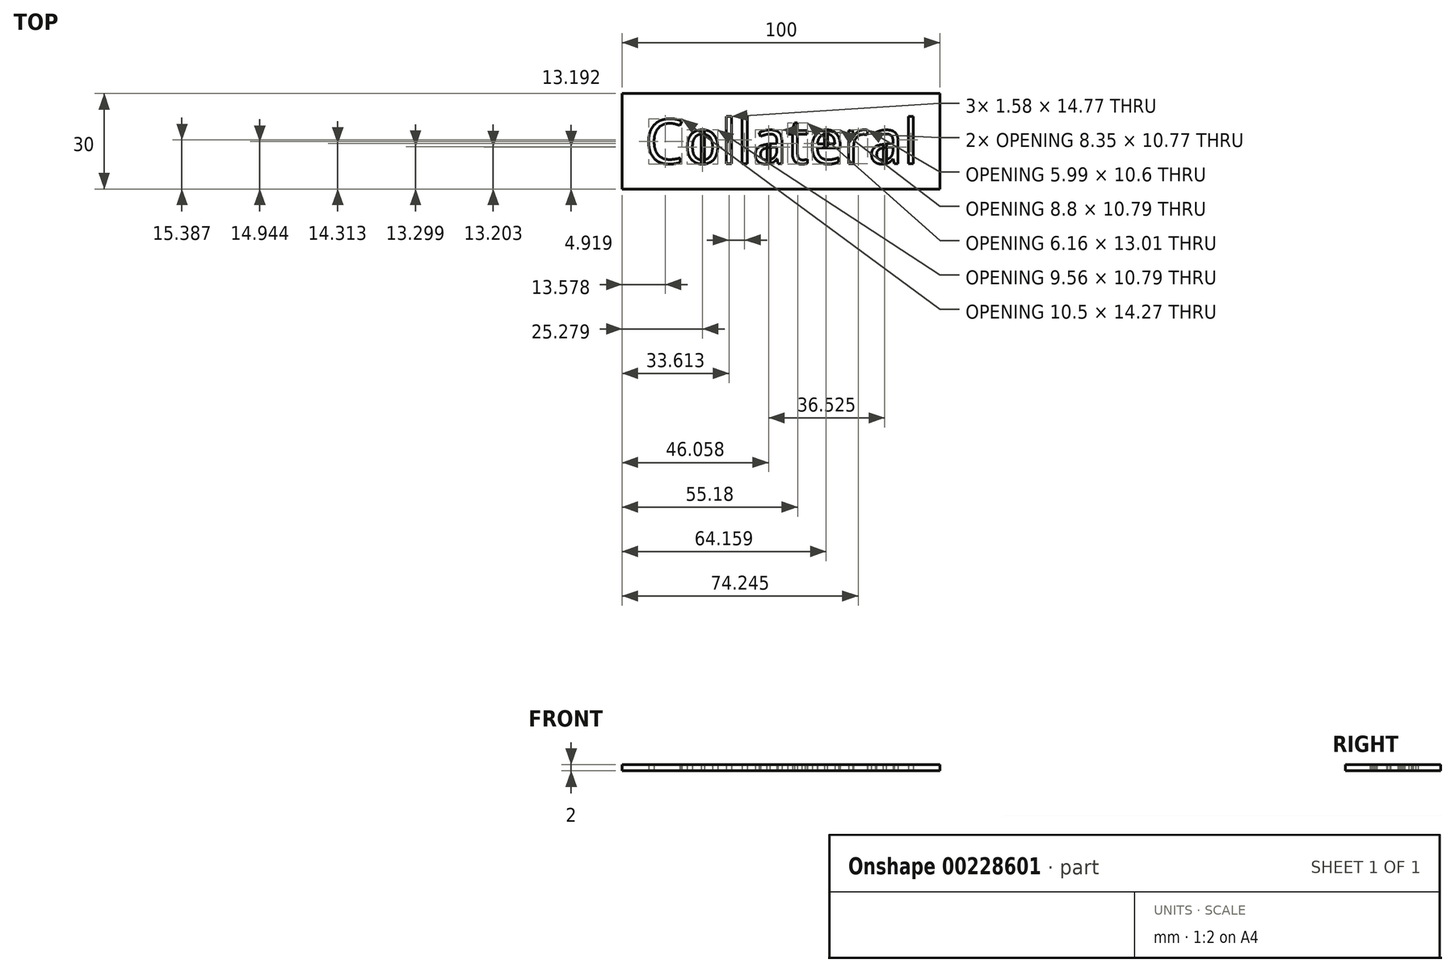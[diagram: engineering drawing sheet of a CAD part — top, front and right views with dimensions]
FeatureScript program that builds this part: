
annotation { "Feature Type Name" : "Feature", "Feature Type Description" : "" }
export const myFeature = defineFeature(function(context is Context, id is Id, definition is map)
    precondition{}
    {
        {
            assignVariable(context, id + "F0", {"name" : "thickness", "anyValue" : 2});
        }
        {
            var Q0;
            Q0=qCreatedBy(makeId("Top.planeOp"),FACE);
            var sketch = newSketch(context, id + "F1", { "sketchPlane" : qUnion([Q0])});
            skText(sketch, "E0", { "text": "Collateral", "fontName": "OpenSans-Regular.ttf"});
            skLineSegment(sketch, "E1.bottom", {"start": v(-51.22, 37.77) * mm, "end": v(48.78, 37.77) * mm});
            skLineSegment(sketch, "E1.top", {"start": v(-51.22, 7.77) * mm, "end": v(48.78, 7.77) * mm});
            skLineSegment(sketch, "E1.left", {"start": v(-51.22, 37.77) * mm, "end": v(-51.22, 7.77) * mm});
            skLineSegment(sketch, "E1.right", {"start": v(48.78, 37.77) * mm, "end": v(48.78, 7.77) * mm});
            const initialGuessF1  = {"E0": [-0.04408, 0.01577, 1, 0, 0.014]};
            skSetInitialGuess(sketch, initialGuessF1);
            skSolve(sketch);
        }
        {
            var Q0;
            Q0=makeQuery(id+"F1.imprint","IMPRINT",FACE,{"disambiguationData":[TD([[makeQuery(id+"F1.imprint","IMPRINT",EDGE,{"derivedFrom":sQuery(id+"F1.wireOp",EDGE,"E0.sketch_text.stroke-0")}),1.0]])]});
            var Q1;
            Q1=makeQuery(id+"F1.imprint","IMPRINT",FACE,{"disambiguationData":[TD([[makeQuery(id+"F1.imprint","IMPRINT",EDGE,{"derivedFrom":sQuery(id+"F1.wireOp",EDGE,"E0.sketch_text.stroke-59")}),1.0]])]});
            var Q2;
            Q2=makeQuery(id+"F1.imprint","IMPRINT",FACE,{"disambiguationData":[TD([[makeQuery(id+"F1.imprint","IMPRINT",EDGE,{"derivedFrom":sQuery(id+"F1.wireOp",EDGE,"E0.sketch_text.stroke-100")}),1.0]])]});
            var Q3;
            Q3=makeQuery(id+"F1.imprint","IMPRINT",FACE,{"disambiguationData":[TD([[makeQuery(id+"F1.imprint","IMPRINT",EDGE,{"derivedFrom":sQuery(id+"F1.wireOp",EDGE,"E0.sketch_text.stroke-137")}),1.0]])]});
            var Q4;
            Q4=makeQuery(id+"F1.imprint","IMPRINT",FACE,{"disambiguationData":[TD([[makeQuery(id+"F1.imprint","IMPRINT",EDGE,{"derivedFrom":sQuery(id+"F1.wireOp",EDGE,"E0.sketch_text.stroke-24")}),1.0]])]});
            extrude(context, id + "F2", {"entities" : qUnion([Q0, Q1, Q2, Q3, Q4]), "depth" : (getVariable(context, 'thickness')) * mm});
        }
        {
            var Q0;
            Q0=makeQuery(id+"F2.opExtrude","CAP_FACE",FACE,{"disambiguationData":[OSD([sQuery(id+"F1.wireOp",EDGE,"E0.sketch_text.stroke-0"),sQuery(id+"F1.wireOp",EDGE,"E0.sketch_text.stroke-1"),sQuery(id+"F1.wireOp",EDGE,"E0.sketch_text.stroke-2"),sQuery(id+"F1.wireOp",EDGE,"E0.sketch_text.stroke-3"),sQuery(id+"F1.wireOp",EDGE,"E0.sketch_text.stroke-4"),sQuery(id+"F1.wireOp",EDGE,"E0.sketch_text.stroke-5"),sQuery(id+"F1.wireOp",EDGE,"E0.sketch_text.stroke-6"),sQuery(id+"F1.wireOp",EDGE,"E0.sketch_text.stroke-7"),sQuery(id+"F1.wireOp",EDGE,"E0.sketch_text.stroke-8"),sQuery(id+"F1.wireOp",EDGE,"E0.sketch_text.stroke-9"),sQuery(id+"F1.wireOp",EDGE,"E0.sketch_text.stroke-10"),sQuery(id+"F1.wireOp",EDGE,"E0.sketch_text.stroke-11"),sQuery(id+"F1.wireOp",EDGE,"E0.sketch_text.stroke-12"),sQuery(id+"F1.wireOp",EDGE,"E0.sketch_text.stroke-13"),sQuery(id+"F1.wireOp",EDGE,"E0.sketch_text.stroke-14"),sQuery(id+"F1.wireOp",EDGE,"E0.sketch_text.stroke-15"),sQuery(id+"F1.wireOp",EDGE,"E0.sketch_text.stroke-16"),sQuery(id+"F1.wireOp",EDGE,"E0.sketch_text.stroke-17"),sQuery(id+"F1.wireOp",EDGE,"E0.sketch_text.stroke-18"),sQuery(id+"F1.wireOp",EDGE,"E0.sketch_text.stroke-19"),sQuery(id+"F1.wireOp",EDGE,"E0.sketch_text.stroke-20"),sQuery(id+"F1.wireOp",EDGE,"E0.sketch_text.stroke-21"),sQuery(id+"F1.wireOp",EDGE,"E0.sketch_text.stroke-22"),sQuery(id+"F1.wireOp",EDGE,"E0.sketch_text.stroke-23"),sQuery(id+"F1.wireOp",EDGE,"E0.sketch_text.stroke-32"),sQuery(id+"F1.wireOp",EDGE,"E0.sketch_text.stroke-33"),sQuery(id+"F1.wireOp",EDGE,"E0.sketch_text.stroke-34"),sQuery(id+"F1.wireOp",EDGE,"E0.sketch_text.stroke-35"),sQuery(id+"F1.wireOp",EDGE,"E0.sketch_text.stroke-36"),sQuery(id+"F1.wireOp",EDGE,"E0.sketch_text.stroke-37"),sQuery(id+"F1.wireOp",EDGE,"E0.sketch_text.stroke-38"),sQuery(id+"F1.wireOp",EDGE,"E0.sketch_text.stroke-39"),sQuery(id+"F1.wireOp",EDGE,"E0.sketch_text.stroke-40"),sQuery(id+"F1.wireOp",EDGE,"E0.sketch_text.stroke-41"),sQuery(id+"F1.wireOp",EDGE,"E0.sketch_text.stroke-42"),sQuery(id+"F1.wireOp",EDGE,"E0.sketch_text.stroke-43"),sQuery(id+"F1.wireOp",EDGE,"E0.sketch_text.stroke-44"),sQuery(id+"F1.wireOp",EDGE,"E0.sketch_text.stroke-45"),sQuery(id+"F1.wireOp",EDGE,"E0.sketch_text.stroke-46"),sQuery(id+"F1.wireOp",EDGE,"E0.sketch_text.stroke-47"),sQuery(id+"F1.wireOp",EDGE,"E0.sketch_text.stroke-48"),sQuery(id+"F1.wireOp",EDGE,"E0.sketch_text.stroke-49"),sQuery(id+"F1.wireOp",EDGE,"E0.sketch_text.stroke-50"),sQuery(id+"F1.wireOp",EDGE,"E0.sketch_text.stroke-51"),sQuery(id+"F1.wireOp",EDGE,"E0.sketch_text.stroke-52"),sQuery(id+"F1.wireOp",EDGE,"E0.sketch_text.stroke-53"),sQuery(id+"F1.wireOp",EDGE,"E0.sketch_text.stroke-54"),sQuery(id+"F1.wireOp",EDGE,"E0.sketch_text.stroke-55"),sQuery(id+"F1.wireOp",EDGE,"E0.sketch_text.stroke-56"),sQuery(id+"F1.wireOp",EDGE,"E0.sketch_text.stroke-57"),sQuery(id+"F1.wireOp",EDGE,"E0.sketch_text.stroke-58"),sQuery(id+"F1.wireOp",EDGE,"E0.sketch_text.stroke-67"),sQuery(id+"F1.wireOp",EDGE,"E0.sketch_text.stroke-68"),sQuery(id+"F1.wireOp",EDGE,"E0.sketch_text.stroke-69"),sQuery(id+"F1.wireOp",EDGE,"E0.sketch_text.stroke-70"),sQuery(id+"F1.wireOp",EDGE,"E0.sketch_text.stroke-71"),sQuery(id+"F1.wireOp",EDGE,"E0.sketch_text.stroke-72"),sQuery(id+"F1.wireOp",EDGE,"E0.sketch_text.stroke-73"),sQuery(id+"F1.wireOp",EDGE,"E0.sketch_text.stroke-74"),sQuery(id+"F1.wireOp",EDGE,"E0.sketch_text.stroke-75"),sQuery(id+"F1.wireOp",EDGE,"E0.sketch_text.stroke-76"),sQuery(id+"F1.wireOp",EDGE,"E0.sketch_text.stroke-77"),sQuery(id+"F1.wireOp",EDGE,"E0.sketch_text.stroke-78"),sQuery(id+"F1.wireOp",EDGE,"E0.sketch_text.stroke-79"),sQuery(id+"F1.wireOp",EDGE,"E0.sketch_text.stroke-80"),sQuery(id+"F1.wireOp",EDGE,"E0.sketch_text.stroke-81"),sQuery(id+"F1.wireOp",EDGE,"E0.sketch_text.stroke-82"),sQuery(id+"F1.wireOp",EDGE,"E0.sketch_text.stroke-83"),sQuery(id+"F1.wireOp",EDGE,"E0.sketch_text.stroke-84"),sQuery(id+"F1.wireOp",EDGE,"E0.sketch_text.stroke-85"),sQuery(id+"F1.wireOp",EDGE,"E0.sketch_text.stroke-86"),sQuery(id+"F1.wireOp",EDGE,"E0.sketch_text.stroke-87"),sQuery(id+"F1.wireOp",EDGE,"E0.sketch_text.stroke-88"),sQuery(id+"F1.wireOp",EDGE,"E0.sketch_text.stroke-89"),sQuery(id+"F1.wireOp",EDGE,"E0.sketch_text.stroke-90"),sQuery(id+"F1.wireOp",EDGE,"E0.sketch_text.stroke-91"),sQuery(id+"F1.wireOp",EDGE,"E0.sketch_text.stroke-92"),sQuery(id+"F1.wireOp",EDGE,"E0.sketch_text.stroke-93"),sQuery(id+"F1.wireOp",EDGE,"E0.sketch_text.stroke-94"),sQuery(id+"F1.wireOp",EDGE,"E0.sketch_text.stroke-95"),sQuery(id+"F1.wireOp",EDGE,"E0.sketch_text.stroke-96"),sQuery(id+"F1.wireOp",EDGE,"E0.sketch_text.stroke-97"),sQuery(id+"F1.wireOp",EDGE,"E0.sketch_text.stroke-98"),sQuery(id+"F1.wireOp",EDGE,"E0.sketch_text.stroke-99"),sQuery(id+"F1.wireOp",EDGE,"E0.sketch_text.stroke-105"),sQuery(id+"F1.wireOp",EDGE,"E0.sketch_text.stroke-106"),sQuery(id+"F1.wireOp",EDGE,"E0.sketch_text.stroke-107"),sQuery(id+"F1.wireOp",EDGE,"E0.sketch_text.stroke-108"),sQuery(id+"F1.wireOp",EDGE,"E0.sketch_text.stroke-109"),sQuery(id+"F1.wireOp",EDGE,"E0.sketch_text.stroke-110"),sQuery(id+"F1.wireOp",EDGE,"E0.sketch_text.stroke-111"),sQuery(id+"F1.wireOp",EDGE,"E0.sketch_text.stroke-112"),sQuery(id+"F1.wireOp",EDGE,"E0.sketch_text.stroke-113"),sQuery(id+"F1.wireOp",EDGE,"E0.sketch_text.stroke-114"),sQuery(id+"F1.wireOp",EDGE,"E0.sketch_text.stroke-115"),sQuery(id+"F1.wireOp",EDGE,"E0.sketch_text.stroke-116"),sQuery(id+"F1.wireOp",EDGE,"E0.sketch_text.stroke-117"),sQuery(id+"F1.wireOp",EDGE,"E0.sketch_text.stroke-118"),sQuery(id+"F1.wireOp",EDGE,"E0.sketch_text.stroke-119"),sQuery(id+"F1.wireOp",EDGE,"E0.sketch_text.stroke-120"),sQuery(id+"F1.wireOp",EDGE,"E0.sketch_text.stroke-121"),sQuery(id+"F1.wireOp",EDGE,"E0.sketch_text.stroke-122"),sQuery(id+"F1.wireOp",EDGE,"E0.sketch_text.stroke-123"),sQuery(id+"F1.wireOp",EDGE,"E0.sketch_text.stroke-124"),sQuery(id+"F1.wireOp",EDGE,"E0.sketch_text.stroke-125"),sQuery(id+"F1.wireOp",EDGE,"E0.sketch_text.stroke-126"),sQuery(id+"F1.wireOp",EDGE,"E0.sketch_text.stroke-127"),sQuery(id+"F1.wireOp",EDGE,"E0.sketch_text.stroke-128"),sQuery(id+"F1.wireOp",EDGE,"E0.sketch_text.stroke-129"),sQuery(id+"F1.wireOp",EDGE,"E0.sketch_text.stroke-130"),sQuery(id+"F1.wireOp",EDGE,"E0.sketch_text.stroke-131"),sQuery(id+"F1.wireOp",EDGE,"E0.sketch_text.stroke-132"),sQuery(id+"F1.wireOp",EDGE,"E0.sketch_text.stroke-133"),sQuery(id+"F1.wireOp",EDGE,"E0.sketch_text.stroke-134"),sQuery(id+"F1.wireOp",EDGE,"E0.sketch_text.stroke-135"),sQuery(id+"F1.wireOp",EDGE,"E0.sketch_text.stroke-136"),sQuery(id+"F1.wireOp",EDGE,"E0.sketch_text.stroke-145"),sQuery(id+"F1.wireOp",EDGE,"E0.sketch_text.stroke-146"),sQuery(id+"F1.wireOp",EDGE,"E0.sketch_text.stroke-147"),sQuery(id+"F1.wireOp",EDGE,"E0.sketch_text.stroke-148"),sQuery(id+"F1.wireOp",EDGE,"E1.bottom"),sQuery(id+"F1.wireOp",EDGE,"E1.top"),sQuery(id+"F1.wireOp",EDGE,"E1.left"),sQuery(id+"F1.wireOp",EDGE,"E1.right")])],"isStart":false});
            var sketch = newSketch(context, id + "F3", { "sketchPlane" : qUnion([Q0])});
            skLineSegment(sketch, "E2.bottom", {"start": v(-26.37, 27.88) * mm, "end": v(-25.37, 27.88) * mm});
            skLineSegment(sketch, "E2.top", {"start": v(-26.37, 13.88) * mm, "end": v(-25.37, 13.88) * mm});
            skLineSegment(sketch, "E2.left", {"start": v(-26.37, 27.88) * mm, "end": v(-26.37, 13.88) * mm});
            skLineSegment(sketch, "E2.right", {"start": v(-25.37, 27.88) * mm, "end": v(-25.37, 13.88) * mm});
            skPoint(sketch, "E2.middle", {"position": v(-25.87, 20.88) * mm});
            skLineSegment(sketch, "E3.bottom", {"start": v(-5.63, 23.16) * mm, "end": v(-4.63, 23.16) * mm});
            skLineSegment(sketch, "E3.top", {"start": v(-5.63, 13.57) * mm, "end": v(-4.63, 13.57) * mm});
            skLineSegment(sketch, "E3.left", {"start": v(-5.63, 23.16) * mm, "end": v(-5.63, 13.57) * mm});
            skLineSegment(sketch, "E3.right", {"start": v(-4.63, 23.16) * mm, "end": v(-4.63, 13.57) * mm});
            skPoint(sketch, "E3.middle", {"position": v(-5.13, 18.36) * mm});
            skLineSegment(sketch, "E4.bottom", {"start": v(12.45, 28.14) * mm, "end": v(13.45, 28.14) * mm});
            skLineSegment(sketch, "E4.top", {"start": v(12.45, 18.73) * mm, "end": v(13.45, 18.73) * mm});
            skLineSegment(sketch, "E4.left", {"start": v(12.45, 28.14) * mm, "end": v(12.45, 18.73) * mm});
            skLineSegment(sketch, "E4.right", {"start": v(13.45, 28.14) * mm, "end": v(13.45, 18.73) * mm});
            skPoint(sketch, "E4.middle", {"position": v(12.95, 23.44) * mm});
            skLineSegment(sketch, "E5.bottom", {"start": v(30.98, 22.96) * mm, "end": v(31.98, 22.96) * mm});
            skLineSegment(sketch, "E5.top", {"start": v(30.98, 14.41) * mm, "end": v(31.98, 14.41) * mm});
            skLineSegment(sketch, "E5.left", {"start": v(30.98, 22.96) * mm, "end": v(30.98, 14.41) * mm});
            skLineSegment(sketch, "E5.right", {"start": v(31.98, 22.96) * mm, "end": v(31.98, 14.41) * mm});
            skPoint(sketch, "E5.middle", {"position": v(31.48, 18.68) * mm});
            skSolve(sketch);
        }
        {
            var Q0;
            {var subQ7=sQuery(id+"F3.wireOp",EDGE,"E2.left");var subQ9=makeQuery(id+"F2.opExtrude","CAP_EDGE",EDGE,{"disambiguationData":[OSD([sQuery(id+"F1.wireOp",EDGE,"E0.sketch_text.stroke-21")])],"isStart":false});var subQ11=makeQuery(id+"F3.imprint","INTERSECT",VERTEX,{"derivedFrom":[subQ9,subQ7]});Q0=makeQuery(id+"F3.imprint","IMPRINT",FACE,{"disambiguationData":[TD([[makeQuery(id+"F3.imprint","IMPRINT",EDGE,{"disambiguationData":[TD([[subQ11,-1.0]])],"derivedFrom":subQ7}),1.0]])]});}
            var Q1;
            {var subQ0=sQuery(id+"F3.wireOp",EDGE,"E3.left");var subQ1=makeQuery(id+"F2.opExtrude","CAP_EDGE",EDGE,{"disambiguationData":[OSD([sQuery(id+"F1.wireOp",EDGE,"E0.sketch_text.stroke-46")])],"isStart":false});var subQ2=makeQuery(id+"F3.imprint","INTERSECT",VERTEX,{"derivedFrom":[subQ1,subQ0]});Q1=makeQuery(id+"F3.imprint","IMPRINT",FACE,{"disambiguationData":[TD([[makeQuery(id+"F3.imprint","IMPRINT",EDGE,{"disambiguationData":[TD([[subQ2,-1.0]])],"derivedFrom":subQ0}),1.0]])]});}
            var Q2;
            {var subQ1=makeQuery(id+"F2.opExtrude","CAP_EDGE",EDGE,{"disambiguationData":[OSD([sQuery(id+"F1.wireOp",EDGE,"E0.sketch_text.stroke-89")])],"isStart":false});var subQ5=sQuery(id+"F3.wireOp",EDGE,"E4.left");var subQ6=makeQuery(id+"F3.imprint","INTERSECT",VERTEX,{"derivedFrom":[subQ1,subQ5]});Q2=makeQuery(id+"F3.imprint","IMPRINT",FACE,{"disambiguationData":[TD([[makeQuery(id+"F3.imprint","IMPRINT",EDGE,{"disambiguationData":[TD([[subQ6,-1.0]])],"derivedFrom":subQ5}),1.0]])]});}
            var Q3;
            {var subQ0=sQuery(id+"F3.wireOp",EDGE,"E5.left");var subQ1=makeQuery(id+"F2.opExtrude","CAP_EDGE",EDGE,{"disambiguationData":[OSD([sQuery(id+"F1.wireOp",EDGE,"E0.sketch_text.stroke-124")])],"isStart":false});var subQ2=makeQuery(id+"F3.imprint","INTERSECT",VERTEX,{"derivedFrom":[subQ1,subQ0]});Q3=makeQuery(id+"F3.imprint","IMPRINT",FACE,{"disambiguationData":[TD([[makeQuery(id+"F3.imprint","IMPRINT",EDGE,{"disambiguationData":[TD([[subQ2,-1.0]])],"derivedFrom":subQ0}),1.0]])]});}
            extrude(context, id + "F4", {"entities" : qUnion([Q0, Q1, Q2, Q3]), "oppositeDirection" : true, "depth" : (getVariable(context, 'thickness')) * mm});
        }
    });
